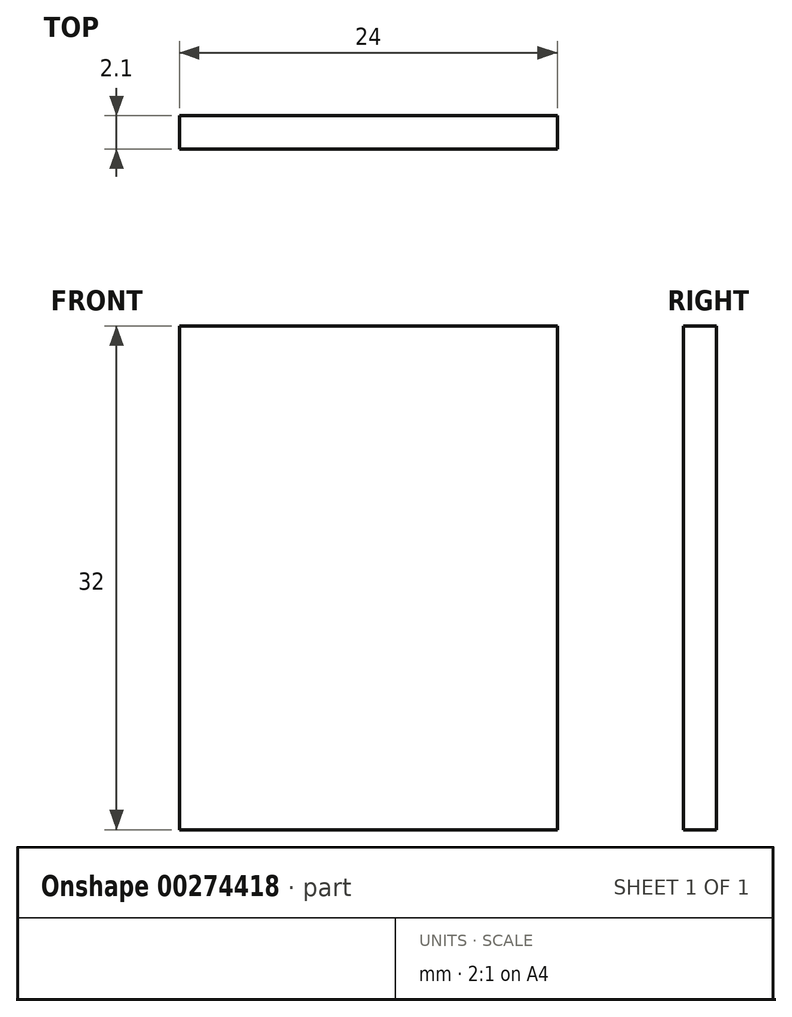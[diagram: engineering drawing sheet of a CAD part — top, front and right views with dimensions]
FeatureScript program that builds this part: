
annotation { "Feature Type Name" : "Feature", "Feature Type Description" : "" }
export const myFeature = defineFeature(function(context is Context, id is Id, definition is map)
    precondition{}
    {
        {
            var Q0;
            Q0=qCreatedBy(makeId("Front.planeOp"),FACE);
            var sketch = newSketch(context, id + "F0", { "sketchPlane" : qUnion([Q0])});
            skLineSegment(sketch, "E0.bottom", {"start": v(-12, 16) * mm, "end": v(12, 16) * mm});
            skLineSegment(sketch, "E0.top", {"start": v(-12, -16) * mm, "end": v(12, -16) * mm});
            skLineSegment(sketch, "E0.left", {"start": v(-12, 16) * mm, "end": v(-12, -16) * mm});
            skLineSegment(sketch, "E0.right", {"start": v(12, 16) * mm, "end": v(12, -16) * mm});
            skPoint(sketch, "E0.middle", {"position": v(0, 0) * mm});
            skSolve(sketch);
        }
        {
            var Q0;
            Q0=makeQuery(id+"F0.imprint","IMPRINT",FACE,{"disambiguationData":[TD([[makeQuery(id+"F0.imprint","IMPRINT",EDGE,{"derivedFrom":sQuery(id+"F0.wireOp",EDGE,"E0.bottom")}),-1.0]])]});
            extrude(context, id + "F1", {"entities" : qUnion([Q0]), "endBound" : BoundingType.SYMMETRIC, "depth" : 2.1 * mm});
        }
    });
